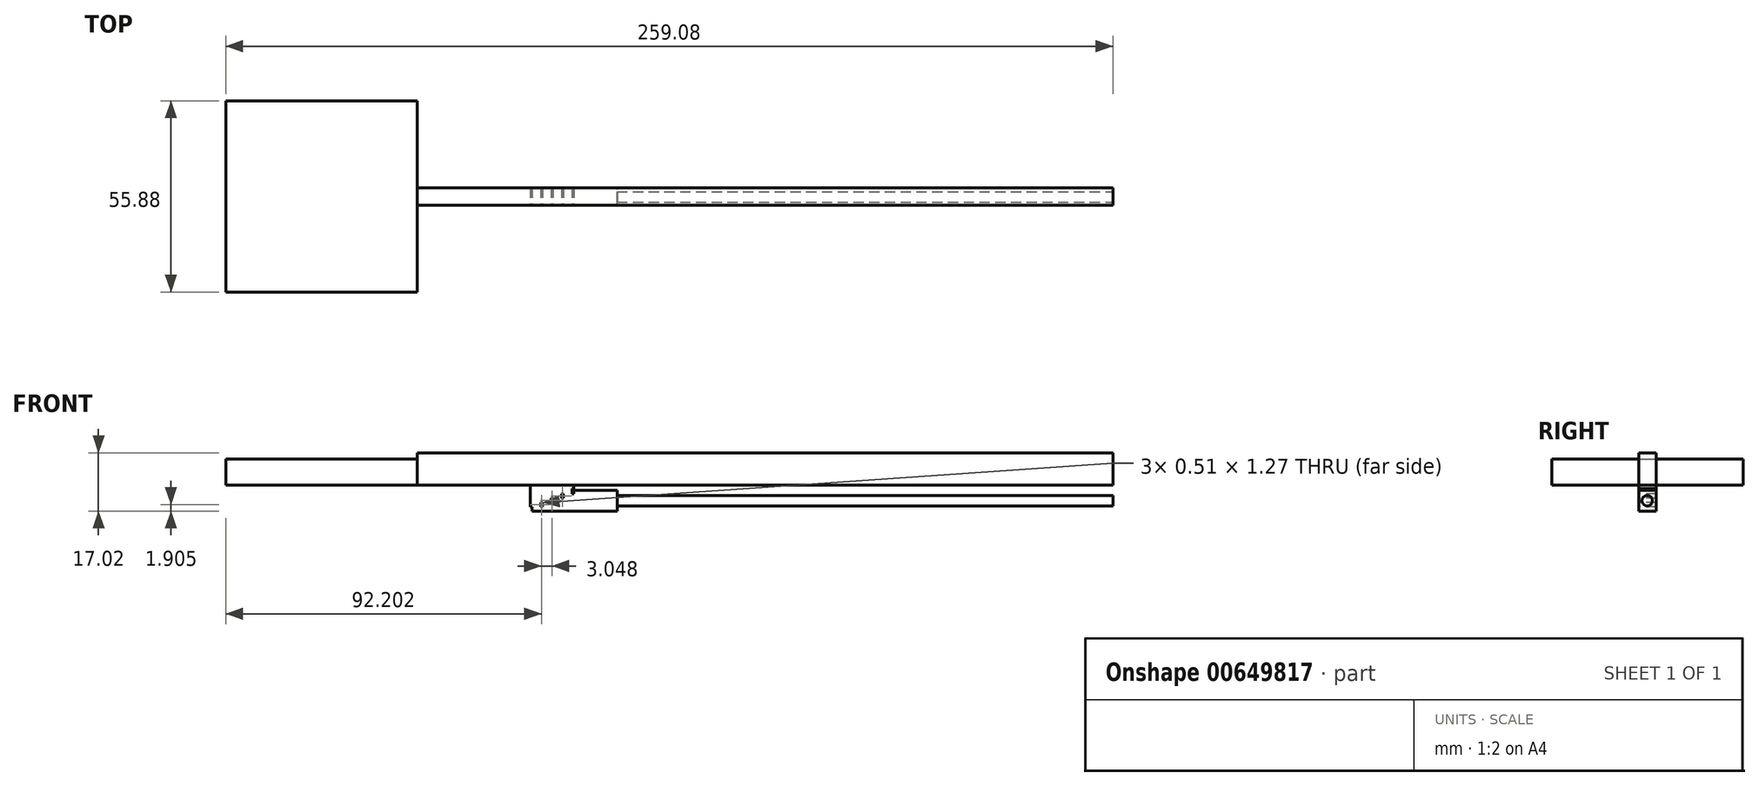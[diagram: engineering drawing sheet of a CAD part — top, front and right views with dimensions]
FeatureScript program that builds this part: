
annotation { "Feature Type Name" : "Feature", "Feature Type Description" : "" }
export const myFeature = defineFeature(function(context is Context, id is Id, definition is map)
    precondition{}
    {
        {
            var Q0;
            Q0=qCreatedBy(makeId("Top.planeOp"),FACE);
            var sketch = newSketch(context, id + "F0", { "sketchPlane" : qUnion([Q0])});
            skLineSegment(sketch, "E0.top", {"start": v(0, 1.52) * mm, "end": v(-6.35, 1.52) * mm});
            skLineSegment(sketch, "E1.bottom", {"start": v(0, 1.52) * mm, "end": v(-25.4, 1.52) * mm});
            skLineSegment(sketch, "E1.top", {"start": v(0, 6.6) * mm, "end": v(-25.4, 6.6) * mm});
            skLineSegment(sketch, "E1.left", {"start": v(0, 1.52) * mm, "end": v(0, 6.6) * mm});
            skLineSegment(sketch, "E1.right", {"start": v(-25.4, 1.52) * mm, "end": v(-25.4, 6.6) * mm});
            skLineSegment(sketch, "E2", {"start": v(-12.7, 6.6) * mm, "end": v(-12.7, 1.52) * mm});
            skSolve(sketch);
        }
        {
            var Q0;
            Q0=qCreatedBy(makeId("Top.planeOp"),FACE);
            cPlane(context, id + "F1", {"entities" : qUnion([Q0]), "cplaneType" : CPlaneType.OFFSET, "offset" : 7.62 * mm, "width" : 152.4 * mm, "height" : 152.4 * mm});
        }
        {
            var Q0;
            Q0=qCreatedBy(id+"F1.planeOp",FACE);
            var sketch = newSketch(context, id + "F2", { "sketchPlane" : qUnion([Q0])});
            skLineSegment(sketch, "E3.bottom", {"start": v(144.78, 1.52) * mm, "end": v(-58.42, 1.52) * mm});
            skLineSegment(sketch, "E3.top", {"start": v(144.78, 6.6) * mm, "end": v(-58.42, 6.6) * mm});
            skLineSegment(sketch, "E3.left", {"start": v(144.78, 1.52) * mm, "end": v(144.78, 6.6) * mm});
            skLineSegment(sketch, "E3.right", {"start": v(-58.42, 1.52) * mm, "end": v(-58.42, 6.6) * mm});
            skSolve(sketch);
        }
        {
            var Q0;
            Q0=makeQuery(id+"F2.imprint","IMPRINT",FACE,{"disambiguationData":[TD([[makeQuery(id+"F2.imprint","IMPRINT",EDGE,{"derivedFrom":sQuery(id+"F2.wireOp",EDGE,"E3.bottom")}),-1.0]])]});
            var Q1;
            Q1=makeQuery(id+"F2.imprint","IMPRINT",FACE,{"disambiguationData":[TD([[makeQuery(id+"F2.imprint","IMPRINT",EDGE,{"derivedFrom":sQuery(id+"F2.wireOp",EDGE,"TAcTqvFI-ZuaQ-72fd-OBFp-i8XLmTCR44Hb.bottom")}),-1.0]])]});
            var Q2;
            Q2=makeQuery(id+"F2.imprint","IMPRINT",FACE,{"disambiguationData":[TD([[makeQuery(id+"F2.imprint","IMPRINT",EDGE,{"derivedFrom":sQuery(id+"F2.wireOp",EDGE,"TAcTqvFI-ZuaQ-72fd-OBFp-i8XLmTCR44Hb.right")}),1.0]])]});
            extrude(context, id + "F3", {"entities" : qUnion([Q0, Q1, Q2]), "depth" : 9.4 * mm, "offsetDistance" : 25.4 * mm});
        }
        {
            var Q0;
            Q0=qCreatedBy(makeId("Top.planeOp"),FACE);
            cPlane(context, id + "F4", {"entities" : qUnion([Q0]), "cplaneType" : CPlaneType.OFFSET, "offset" : 17.78 * mm, "width" : 152.4 * mm, "height" : 152.4 * mm});
        }
        {
            var Q0;
            Q0=qCreatedBy(id+"F4.planeOp",FACE);
            var sketch = newSketch(context, id + "F5", { "sketchPlane" : qUnion([Q0])});
            skSolve(sketch);
        }
        {
            var Q0;
            Q0=qCreatedBy(makeId("Top.planeOp"),FACE);
            cPlane(context, id + "F6", {"entities" : qUnion([Q0]), "cplaneType" : CPlaneType.OFFSET, "offset" : 22.86 * mm, "width" : 152.4 * mm, "height" : 152.4 * mm});
        }
        {
            var Q0;
            Q0=qCreatedBy(id+"F6.planeOp",FACE);
            var sketch = newSketch(context, id + "F7", { "sketchPlane" : qUnion([Q0])});
            skSolve(sketch);
        }
        {
            var Q0;
            Q0=qCreatedBy(makeId("Front.planeOp"),FACE);
            cPlane(context, id + "F8", {"entities" : qUnion([Q0]), "cplaneType" : CPlaneType.OFFSET, "offset" : 8.25 * mm, "width" : 152.4 * mm, "height" : 152.4 * mm});
        }
        {
            var Q0;
            Q0=qCreatedBy(makeId("Front.planeOp"),FACE);
            cPlane(context, id + "F9", {"entities" : qUnion([Q0]), "cplaneType" : CPlaneType.OFFSET, "offset" : 1.9 * mm, "width" : 152.4 * mm, "height" : 152.4 * mm});
        }
        {
            var Q0;
            Q0=qCreatedBy(makeId("Front.planeOp"),FACE);
            cPlane(context, id + "F10", {"entities" : qUnion([Q0]), "cplaneType" : CPlaneType.OFFSET, "offset" : 4.06 * mm, "oppositeDirection" : true, "width" : 152.4 * mm, "height" : 152.4 * mm});
        }
        {
            var Q0;
            Q0=qCreatedBy(id+"F10.planeOp",FACE);
            var sketch = newSketch(context, id + "F11", { "sketchPlane" : qUnion([Q0])});
            skLineSegment(sketch, "E4.bottom", {"start": v(-12.7, 6.6) * mm, "end": v(-13.2, 6.6) * mm});
            skLineSegment(sketch, "E4.top", {"start": v(-12.7, 5.08) * mm, "end": v(-13.2, 5.08) * mm});
            skLineSegment(sketch, "E4.left", {"start": v(-12.7, 6.6) * mm, "end": v(-12.7, 5.08) * mm});
            skLineSegment(sketch, "E4.right", {"start": v(-13.2, 6.6) * mm, "end": v(-13.2, 5.08) * mm});
            skLineSegment(sketch, "E5.bottom", {"start": v(-25.4, 0) * mm, "end": v(-24.9, 0) * mm});
            skLineSegment(sketch, "E5.top", {"start": v(-25.4, 1.27) * mm, "end": v(-24.9, 1.27) * mm});
            skLineSegment(sketch, "E5.left", {"start": v(-25.4, 0) * mm, "end": v(-25.4, 1.27) * mm});
            skLineSegment(sketch, "E5.right", {"start": v(-24.9, 0) * mm, "end": v(-24.9, 1.27) * mm});
            skLineSegment(sketch, "E6.bottom", {"start": v(-18.8, 3.81) * mm, "end": v(-19.3, 3.81) * mm});
            skLineSegment(sketch, "E6.top", {"start": v(-18.8, 2.54) * mm, "end": v(-19.3, 2.54) * mm});
            skLineSegment(sketch, "E6.left", {"start": v(-18.8, 3.81) * mm, "end": v(-18.8, 2.54) * mm});
            skLineSegment(sketch, "E6.right", {"start": v(-19.3, 3.81) * mm, "end": v(-19.3, 2.54) * mm});
            skPoint(sketch, "E6.middle", {"position": v(-19.05, 3.17) * mm});
            skLineSegment(sketch, "E7.bottom", {"start": v(-15.75, 5.08) * mm, "end": v(-16.26, 5.08) * mm});
            skLineSegment(sketch, "E7.top", {"start": v(-15.75, 3.8) * mm, "end": v(-16.26, 3.8) * mm});
            skLineSegment(sketch, "E7.left", {"start": v(-15.75, 5.08) * mm, "end": v(-15.75, 3.8) * mm});
            skLineSegment(sketch, "E7.right", {"start": v(-16.26, 5.08) * mm, "end": v(-16.26, 3.8) * mm});
            skPoint(sketch, "E7.middle", {"position": v(-16, 4.45) * mm});
            skLineSegment(sketch, "E8.bottom", {"start": v(-21.84, 2.54) * mm, "end": v(-22.35, 2.54) * mm});
            skLineSegment(sketch, "E8.top", {"start": v(-21.84, 1.27) * mm, "end": v(-22.35, 1.27) * mm});
            skLineSegment(sketch, "E8.left", {"start": v(-21.84, 2.54) * mm, "end": v(-21.84, 1.27) * mm});
            skLineSegment(sketch, "E8.right", {"start": v(-22.35, 2.54) * mm, "end": v(-22.35, 1.27) * mm});
            skPoint(sketch, "E8.middle", {"position": v(-22.1, 1.9) * mm});
            skSolve(sketch);
        }
        {
            var Q0;
            {var subQ0=sQuery(id+"F0.wireOp",EDGE,"E1.right");Q0=makeQuery(id+"F0.imprint","IMPRINT",FACE,{"disambiguationData":[TD([[makeQuery(id+"F0.imprint","IMPRINT",EDGE,{"derivedFrom":subQ0}),-1.0]])]});}
            extrude(context, id + "F12", {"entities" : qUnion([Q0]), "depth" : 7.62 * mm, "offsetDistance" : 25.4 * mm});
        }
        {
            var Q0;
            Q0=qSketchRegion(id+"F11",true);
            extrude(context, id + "F13", {"entities" : qUnion([Q0]), "operationType" : NewBodyOperationType.REMOVE, "endBound" : BoundingType.SYMMETRIC, "oppositeDirection" : true, "depth" : 5.08 * mm, "offsetDistance" : 25.4 * mm});
        }
        {
            var Q0;
            Q0=qCreatedBy(id+"F4.planeOp",FACE);
            var sketch = newSketch(context, id + "F14", { "sketchPlane" : qUnion([Q0])});
            skSolve(sketch);
        }
        {
            var Q0;
            Q0=qCreatedBy(id+"F1.planeOp",FACE);
            var sketch = newSketch(context, id + "F15", { "sketchPlane" : qUnion([Q0])});
            skLineSegment(sketch, "E9.bottom", {"start": v(-58.42, -23.88) * mm, "end": v(-114.3, -23.88) * mm});
            skLineSegment(sketch, "E9.top", {"start": v(-58.42, 32) * mm, "end": v(-114.3, 32) * mm});
            skLineSegment(sketch, "E9.left", {"start": v(-58.42, -23.88) * mm, "end": v(-58.42, 32) * mm});
            skLineSegment(sketch, "E9.right", {"start": v(-114.3, -23.88) * mm, "end": v(-114.3, 32) * mm});
            skSolve(sketch);
        }
        {
            var Q0;
            Q0=makeQuery(id+"F15.imprint","IMPRINT",FACE,{"disambiguationData":[TD([[makeQuery(id+"F15.imprint","IMPRINT",EDGE,{"derivedFrom":sQuery(id+"F15.wireOp",EDGE,"E9.bottom")}),-1.0]])]});
            extrude(context, id + "F16", {"entities" : qUnion([Q0]), "operationType" : NewBodyOperationType.ADD, "depth" : 7.62 * mm, "offsetDistance" : 30.48 * mm});
        }
        {
            var Q0;
            {var subQ0=sQuery(id+"F0.wireOp",EDGE,"E1.left");Q0=makeQuery(id+"F0.imprint","IMPRINT",FACE,{"disambiguationData":[TD([[makeQuery(id+"F0.imprint","IMPRINT",EDGE,{"derivedFrom":subQ0}),1.0]])]});}
            extrude(context, id + "F17", {"entities" : qUnion([Q0]), "operationType" : NewBodyOperationType.ADD, "depth" : 6.1 * mm, "offsetDistance" : 30.48 * mm});
        }
        {
            var Q0;
            Q0=qCreatedBy(makeId("Right.planeOp"),FACE);
            var sketch = newSketch(context, id + "F18", { "sketchPlane" : qUnion([Q0])});
            skCircle(sketch, "E10", {"center": v(3.96, 3.05) * mm, "radius": 1.52 * mm});
            skSolve(sketch);
        }
        {
            var Q0;
            Q0=qCreatedBy(makeId("Front.planeOp"),FACE);
            cPlane(context, id + "F19", {"entities" : qUnion([Q0]), "cplaneType" : CPlaneType.OFFSET, "offset" : 3.96 * mm, "oppositeDirection" : true, "width" : 152.4 * mm, "height" : 152.4 * mm});
        }
        {
            var Q0;
            Q0=qCreatedBy(id+"F19.planeOp",FACE);
            var sketch = newSketch(context, id + "F20", { "sketchPlane" : qUnion([Q0])});
            skLineSegment(sketch, "E11", {"start": v(0, 3.05) * mm, "end": v(144.78, 3.05) * mm});
            skSolve(sketch);
        }
        {
            var Q0;
            Q0=makeQuery(id+"F18.imprint","IMPRINT",FACE,{"disambiguationData":[TD([[makeQuery(id+"F18.imprint","IMPRINT",EDGE,{"derivedFrom":sQuery(id+"F18.wireOp",EDGE,"E10")}),1.0]])]});
            var Q1;
            Q1=sQuery(id+"F18.wireOp",EDGE,"E10");
            var Q2;
            Q2=sQuery(id+"F20.wireOp",EDGE,"E11");
            sweep(context, id + "F21", {"profiles" : qUnion([Q0]), "surfaceProfiles" : qUnion([Q1]), "path" : qUnion([Q2])});
        }
    });
